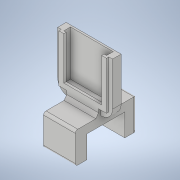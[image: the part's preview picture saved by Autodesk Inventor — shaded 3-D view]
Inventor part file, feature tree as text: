
AUTODESK INVENTOR PART (.ipt)
format: ipt  version: 2022 (Build 260153000, 153)  size: 249,344 bytes
history: native  units: mm
features: extrude x10, sketch x10, fillet x2
ambient origin geometry x8: Origin, YZ Plane, XZ Plane, XY Plane, X Axis, Y Axis, Z Axis, Center Point
bodies: Solid1 (feature_tree)
feature tree (22):
  extrude  "Extrusion1"  Depth=50.0mm
  extrude  "Extrusion2"  Depth=42.0mm
  extrude  "Extrusion6"  Depth=31.0mm
  fillet  "Fillet1"  Radius=31.0mm
  extrude  "Extrusion8"  Depth=7.0mm
  extrude  "Extrusion9"  Depth=6.0mm
  extrude  "Extrusion10"  Depth=25.4mm TaperAngle=0.0deg
  extrude  "Extrusion11"  Depth=2.0mm
  extrude  "Extrusion12"  Depth=4.0mm
  fillet  "Fillet2"  Radius=3.0mm
  extrude  "Extrusion13"  Depth=45.0mm
  extrude  "Extrusion14"  Depth=37.0mm TaperAngle=0.0deg
  sketch  "Sketch1"  dims[d0=25.4mm d1=50.0mm]
  sketch  "Sketch2"  dims[d2=5.0mm d3=0.0mm d4=42.0mm]
  sketch  "Sketch6"  dims[d5=15.2mm d6=37.5mm d7=31.0mm]
  sketch  "Sketch8"  dims[d8=21.0mm d9=0.0mm d14=7.0mm]
  sketch  "Sketch9"  dims[d24=6.0mm d25=9.55mm]
  sketch  "Sketch10"  dims[d26=18.0mm d27=25.4mm d28=0.0mm]
  sketch  "Sketch11"  dims[d29=2.0mm d33=22.5mm]
  sketch  "Sketch12"  dims[d34=22.5mm d35=4.0mm d36=3.0mm]
  sketch  "Sketch13"  dims[d37=45.0mm d38=0.0mm d39=17.5mm]
  sketch  "Sketch14"  dims[d40=17.5mm d41=37.0mm d42=0.0mm d43=2.0mm d44=0.0mm d45=2.0mm d46=2.0mm d48=2.0mm d49=35.0mm d50=31.0mm d51=2.0mm d52=0.0mm d53=3.0mm d54=0.0mm d55=9.5mm d56=6.108652mm d57=6.108652mm d58=3.0mm d59=0.0mm d60=0.0mm d61=0.0mm]
